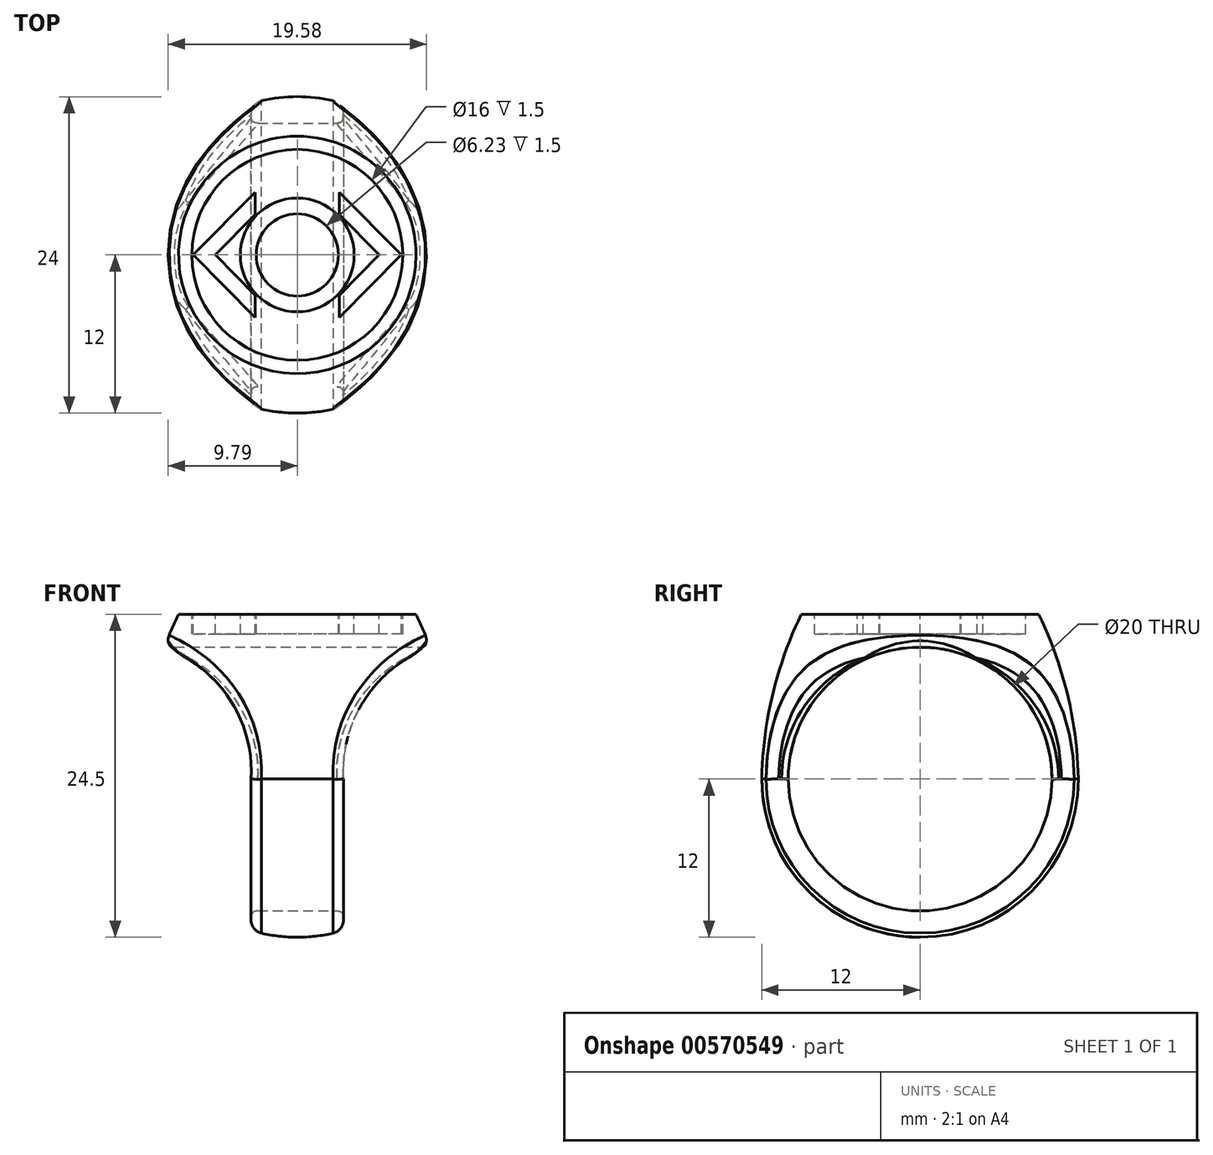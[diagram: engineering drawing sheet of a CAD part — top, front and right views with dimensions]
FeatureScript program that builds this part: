
annotation { "Feature Type Name" : "Feature", "Feature Type Description" : "" }
export const myFeature = defineFeature(function(context is Context, id is Id, definition is map)
    precondition{}
    {
        {
            var Q0;
            Q0=qCreatedBy(makeId("Right.planeOp"),FACE);
            var sketch = newSketch(context, id + "F0", { "sketchPlane" : qUnion([Q0])});
            skLineSegment(sketch, "E0", {"start": v(0, 0) * mm, "end": v(0, -24.5) * mm});
            skLineSegment(sketch, "E1", {"start": v(0, 0) * mm, "end": v(-9, 0) * mm});
            skArc(sketch, "E2", {"start": v(-12, -12.5) * mm, "mid": v(-8.49, -20.99) * mm, "end": v(0, -24.5) * mm});
            skLineSegment(sketch, "E3", {"start": v(0, -12.5) * mm, "end": v(-12, -12.5) * mm, "construction": true});
            skArc(sketch, "E4", {"start": v(-9, 0) * mm, "mid": v(-11.18, -6.09) * mm, "end": v(-12, -12.5) * mm});
            skSolve(sketch);
        }
        {
            var Q0;
            Q0=makeQuery(id+"F0.imprint","IMPRINT",FACE,{"disambiguationData":[TD([[makeQuery(id+"F0.imprint","IMPRINT",EDGE,{"derivedFrom":sQuery(id+"F0.wireOp",EDGE,"E0")}),-1.0]])]});
            var Q1;
            Q1=sQuery(id+"F0.wireOp",EDGE,"E0");
            revolve(context, id + "F1", {"entities" : qUnion([Q0]), "axis" : qUnion([Q1]), "revolveType" : RevolveType.FULL});
        }
        {
            var Q0;
            Q0=qCreatedBy(makeId("Right.planeOp"),FACE);
            var sketch = newSketch(context, id + "F2", { "sketchPlane" : qUnion([Q0])});
            skCircle(sketch, "E5", {"center": v(0, -12.5) * mm, "radius": 10 * mm});
            skSolve(sketch);
        }
        {
            var Q0;
            Q0=qSketchRegion(id+"F2",true);
            extrude(context, id + "F3", {"entities" : qUnion([Q0]), "operationType" : NewBodyOperationType.REMOVE, "oppositeDirection" : true, "depth" : 25 * mm, "offsetDistance" : 25 * mm, "symmetric" : true});
        }
        {
            var Q0;
            Q0=qCreatedBy(makeId("Front.planeOp"),FACE);
            var sketch = newSketch(context, id + "F4", { "sketchPlane" : qUnion([Q0])});
            skLineSegment(sketch, "E6", {"start": v(3.5, -26.5) * mm, "end": v(3.5, -12.5) * mm});
            skArc(sketch, "E7", {"start": v(10.15, -2.5) * mm, "mid": v(5.16, -6.39) * mm, "end": v(3.5, -12.5) * mm});
            skLineSegment(sketch, "E8", {"start": v(10.15, -2.5) * mm, "end": v(11.65, -2.5) * mm});
            skLineSegment(sketch, "E9", {"start": v(11.65, -2.5) * mm, "end": v(11.65, -26.5) * mm});
            skLineSegment(sketch, "E10", {"start": v(11.65, -26.5) * mm, "end": v(3.5, -26.5) * mm});
            skPoint(sketch, "E11.start.orphan", {"position": v(0, -24.5) * mm});
            skLineSegment(sketch, "E12", {"start": v(0, 0) * mm, "end": v(0, -24.5) * mm, "construction": true});
            skLineSegment(sketch, "E13.MirrorCS", {"start": v(-3.5, -26.5) * mm, "end": v(-3.5, -12.5) * mm});
            skArc(sketch, "E14.MirrorCS", {"start": v(-10.15, -2.5) * mm, "mid": v(-5.16, -6.39) * mm, "end": v(-3.5, -12.5) * mm});
            skLineSegment(sketch, "E15.MirrorCS", {"start": v(-11.65, -2.5) * mm, "end": v(-11.65, -26.5) * mm});
            skLineSegment(sketch, "E16.MirrorCS", {"start": v(-11.65, -26.5) * mm, "end": v(-3.5, -26.5) * mm});
            skLineSegment(sketch, "E17.MirrorCS", {"start": v(-10.15, -2.5) * mm, "end": v(-11.65, -2.5) * mm});
            skSolve(sketch);
        }
        {
            var Q0;
            Q0=qSketchRegion(id+"F4",true);
            extrude(context, id + "F5", {"entities" : qUnion([Q0]), "operationType" : NewBodyOperationType.REMOVE, "depth" : 25 * mm, "offsetDistance" : 25 * mm, "symmetric" : true});
        }
        {
            var Q0;
            Q0=makeQuery(id+"F1.opRevolve","SWEPT_FACE",FACE,{"disambiguationData":[OSD([sQuery(id+"F0.wireOp",EDGE,"E1")])]});
            var sketch = newSketch(context, id + "F6", { "sketchPlane" : qUnion([Q0])});
            skCircle(sketch, "E18", {"center": v(0, 0) * mm, "radius": 8 * mm});
            skLineSegment(sketch, "E19", {"start": v(-8, 0) * mm, "end": v(8, 0) * mm, "construction": true});
            skArc(sketch, "E20", {"start": v(3.11, 0) * mm, "mid": v(0, 3.11) * mm, "end": v(-3.11, 0) * mm});
            skArc(sketch, "E21", {"start": v(4.31, 0) * mm, "mid": v(0, 4.31) * mm, "end": v(-4.31, 0) * mm});
            skLineSegment(sketch, "E22", {"start": v(0, 8) * mm, "end": v(0, -8) * mm, "construction": true});
            skArc(sketch, "E23", {"start": v(4.31, 0) * mm, "mid": v(0, -4.31) * mm, "end": v(-4.31, 0) * mm});
            skArc(sketch, "E24", {"start": v(3.11, 0) * mm, "mid": v(0, -3.11) * mm, "end": v(-3.11, 0) * mm});
            skLineSegment(sketch, "E25", {"start": v(3.18, 4.76) * mm, "end": v(3.18, 3.05) * mm});
            skLineSegment(sketch, "E26", {"start": v(6.21, 0) * mm, "end": v(3.18, -3.05) * mm});
            skLineSegment(sketch, "E27", {"start": v(6.21, 0) * mm, "end": v(3.18, 3.05) * mm});
            skLineSegment(sketch, "E28.trimOffspring", {"start": v(3.18, -3.05) * mm, "end": v(3.18, -4.76) * mm});
            skLineSegment(sketch, "E29", {"start": v(3.18, -4.76) * mm, "end": v(7.9, 0) * mm});
            skLineSegment(sketch, "E30", {"start": v(7.9, 0) * mm, "end": v(3.18, 4.76) * mm});
            skLineSegment(sketch, "E31.MirrorCS", {"start": v(-3.18, 4.76) * mm, "end": v(-3.18, 3.05) * mm});
            skLineSegment(sketch, "E32.MirrorCS", {"start": v(-7.9, 0) * mm, "end": v(-3.18, 4.76) * mm});
            skLineSegment(sketch, "E33.MirrorCS", {"start": v(-6.21, 0) * mm, "end": v(-3.18, 3.05) * mm});
            skLineSegment(sketch, "E34.MirrorCS", {"start": v(-6.21, 0) * mm, "end": v(-3.18, -3.05) * mm});
            skLineSegment(sketch, "E35.MirrorCS", {"start": v(-3.18, -4.76) * mm, "end": v(-7.9, 0) * mm});
            skLineSegment(sketch, "E36.MirrorCS", {"start": v(-3.18, -3.05) * mm, "end": v(-3.18, -4.76) * mm});
            skSolve(sketch);
        }
        {
            var Q0;
            Q0=makeQuery(id+"F6.imprint","IMPRINT",FACE,{"disambiguationData":[TD([[makeQuery(id+"F6.imprint","IMPRINT",EDGE,{"derivedFrom":sQuery(id+"F6.wireOp",EDGE,"E20")}),1.0]])]});
            var Q1;
            Q1=makeQuery(id+"F6.imprint","IMPRINT",FACE,{"disambiguationData":[TD([[makeQuery(id+"F6.imprint","IMPRINT",EDGE,{"derivedFrom":sQuery(id+"F6.wireOp",EDGE,"E18")}),1.0]])]});
            extrude(context, id + "F7", {"entities" : qUnion([Q0, Q1]), "operationType" : NewBodyOperationType.REMOVE, "oppositeDirection" : true, "depth" : 1.5 * mm, "offsetDistance" : 25 * mm});
        }
        {
            var Q0;
            Q0=makeQuery(id+"F5.boolean.opBoolean","INTERSECT",EDGE,{"disambiguationData":[OD(1.0)],"derivedFrom":[makeQuery(id+"F1.opRevolve","SWEPT_FACE",FACE,{"disambiguationData":[OSD([sQuery(id+"F0.wireOp",EDGE,"E4")])]}),makeQuery(id+"F5.opExtrude","SWEPT_FACE",FACE,{"disambiguationData":[OSD([sQuery(id+"F4.wireOp",EDGE,"E14.MirrorCS")])]})]});
            var Q1;
            Q1=makeQuery(id+"F5.boolean.opBoolean","INTERSECT",EDGE,{"derivedFrom":[makeQuery(id+"F1.opRevolve","SWEPT_FACE",FACE,{"disambiguationData":[OSD([sQuery(id+"F0.wireOp",EDGE,"E2")])]}),makeQuery(id+"F5.opExtrude","SWEPT_FACE",FACE,{"disambiguationData":[OSD([sQuery(id+"F4.wireOp",EDGE,"E13.MirrorCS")])]})]});
            var Q2;
            Q2=makeQuery(id+"F5.boolean.opBoolean","INTERSECT",EDGE,{"disambiguationData":[OD(1.0)],"derivedFrom":[makeQuery(id+"F1.opRevolve","SWEPT_FACE",FACE,{"disambiguationData":[OSD([sQuery(id+"F0.wireOp",EDGE,"E4")])]}),makeQuery(id+"F5.opExtrude","SWEPT_FACE",FACE,{"disambiguationData":[OSD([sQuery(id+"F4.wireOp",EDGE,"E7")])]})]});
            var Q3;
            Q3=makeQuery(id+"F5.boolean.opBoolean","INTERSECT",EDGE,{"derivedFrom":[makeQuery(id+"F1.opRevolve","SWEPT_FACE",FACE,{"disambiguationData":[OSD([sQuery(id+"F0.wireOp",EDGE,"E2")])]}),makeQuery(id+"F5.opExtrude","SWEPT_FACE",FACE,{"disambiguationData":[OSD([sQuery(id+"F4.wireOp",EDGE,"E6")])]})]});
            fillet(context, id + "F8", {"entities" : qUnion([Q0, Q1, Q2, Q3]), "radius" : 1 * mm, "allowEdgeOverflow" : false});
        }
        {
            var Q0;
            Q0=makeQuery(id+"F5.boolean.opBoolean","INTERSECT",EDGE,{"disambiguationData":[OD(1.0)],"derivedFrom":[makeQuery(id+"F3.boolean.opBoolean","COPY",FACE,{"derivedFrom":makeQuery(id+"F3.opExtrude","SWEPT_FACE",FACE,{"disambiguationData":[OSD([sQuery(id+"F2.wireOp",EDGE,"E5")])]})}),makeQuery(id+"F5.opExtrude","SWEPT_FACE",FACE,{"disambiguationData":[OSD([sQuery(id+"F4.wireOp",EDGE,"E14.MirrorCS")])]})]});
            var Q1;
            Q1=makeQuery(id+"F5.boolean.opBoolean","INTERSECT",EDGE,{"derivedFrom":[makeQuery(id+"F3.boolean.opBoolean","COPY",FACE,{"derivedFrom":makeQuery(id+"F3.opExtrude","SWEPT_FACE",FACE,{"disambiguationData":[OSD([sQuery(id+"F2.wireOp",EDGE,"E5")])]})}),makeQuery(id+"F5.opExtrude","SWEPT_FACE",FACE,{"disambiguationData":[OSD([sQuery(id+"F4.wireOp",EDGE,"E13.MirrorCS")])]})]});
            var Q2;
            Q2=makeQuery(id+"F5.boolean.opBoolean","INTERSECT",EDGE,{"disambiguationData":[OD(0.0)],"derivedFrom":[makeQuery(id+"F3.boolean.opBoolean","COPY",FACE,{"derivedFrom":makeQuery(id+"F3.opExtrude","SWEPT_FACE",FACE,{"disambiguationData":[OSD([sQuery(id+"F2.wireOp",EDGE,"E5")])]})}),makeQuery(id+"F5.opExtrude","SWEPT_FACE",FACE,{"disambiguationData":[OSD([sQuery(id+"F4.wireOp",EDGE,"E14.MirrorCS")])]})]});
            var Q3;
            Q3=makeQuery(id+"F5.boolean.opBoolean","INTERSECT",EDGE,{"disambiguationData":[OD(0.0)],"derivedFrom":[makeQuery(id+"F3.boolean.opBoolean","COPY",FACE,{"derivedFrom":makeQuery(id+"F3.opExtrude","SWEPT_FACE",FACE,{"disambiguationData":[OSD([sQuery(id+"F2.wireOp",EDGE,"E5")])]})}),makeQuery(id+"F5.opExtrude","SWEPT_FACE",FACE,{"disambiguationData":[OSD([sQuery(id+"F4.wireOp",EDGE,"E7")])]})]});
            var Q4;
            Q4=makeQuery(id+"F3.boolean.opBoolean","COPY",FACE,{"derivedFrom":makeQuery(id+"F3.opExtrude","SWEPT_FACE",FACE,{"disambiguationData":[OSD([sQuery(id+"F2.wireOp",EDGE,"E5")])]})});
            fillet(context, id + "F9", {"entities" : qUnion([Q0, Q1, Q2, Q3, Q4]), "radius" : .5 * mm, "rho" : 0.5, "crossSection" : FilletCrossSection.CONIC, "allowEdgeOverflow" : false});
        }
    });
